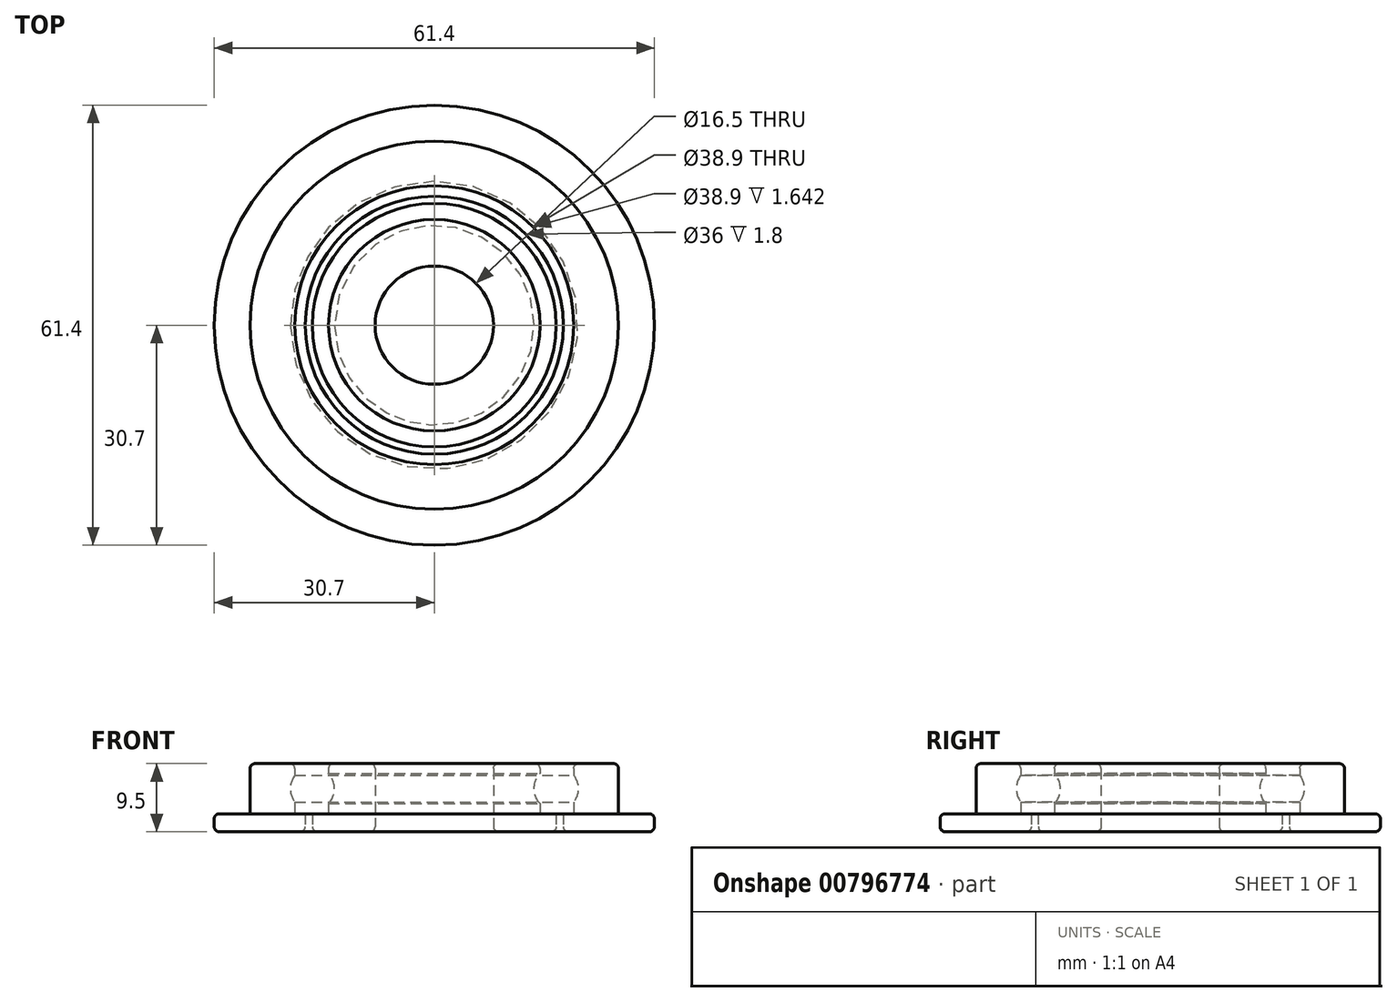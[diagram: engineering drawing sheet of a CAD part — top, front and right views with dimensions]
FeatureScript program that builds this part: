
annotation { "Feature Type Name" : "Feature", "Feature Type Description" : "" }
export const myFeature = defineFeature(function(context is Context, id is Id, definition is map)
    precondition{}
    {
        {
            var Q0;
            Q0=qCreatedBy(makeId("Front.planeOp"),FACE);
            var sketch = newSketch(context, id + "F0", { "sketchPlane" : qUnion([Q0])});
            skLineSegment(sketch, "E0.bottom", {"start": v(8.25, 3.5) * mm, "end": v(14.75, 3.5) * mm});
            skLineSegment(sketch, "E0.top", {"start": v(8.25, -3.5) * mm, "end": v(14.75, -3.5) * mm});
            skLineSegment(sketch, "E0.left", {"start": v(8.25, 3.5) * mm, "end": v(8.25, -3.5) * mm});
            skLineSegment(sketch, "E0.right", {"start": v(14.75, 3.5) * mm, "end": v(14.75, -3.5) * mm});
            skLineSegment(sketch, "E1.bottom", {"start": v(19.45, -3.5) * mm, "end": v(25.7, -3.5) * mm});
            skLineSegment(sketch, "E1.top", {"start": v(19.45, 3.5) * mm, "end": v(25.7, 3.5) * mm});
            skLineSegment(sketch, "E1.left", {"start": v(19.45, -3.5) * mm, "end": v(19.45, 3.5) * mm});
            skLineSegment(sketch, "E1.right", {"start": v(25.7, -3.5) * mm, "end": v(25.7, 3.5) * mm});
            skCircle(sketch, "E2", {"center": v(17, 0) * mm, "radius": 3.08 * mm});
            skLineSegment(sketch, "E3", {"start": v(0, 0) * mm, "end": v(0, 9.43) * mm, "construction": true});
            skLineSegment(sketch, "E4.bottom", {"start": v(8.25, -3.5) * mm, "end": v(17, -3.5) * mm});
            skLineSegment(sketch, "E4.top", {"start": v(8.25, -6) * mm, "end": v(17, -6) * mm});
            skLineSegment(sketch, "E4.left", {"start": v(8.25, -3.5) * mm, "end": v(8.25, -6) * mm});
            skLineSegment(sketch, "E4.right", {"start": v(17, -3.5) * mm, "end": v(17, -6) * mm});
            skLineSegment(sketch, "E5.bottom", {"start": v(8.25, 3.5) * mm, "end": v(10.25, 3.5) * mm});
            skLineSegment(sketch, "E5.top", {"start": v(8.25, 8.5) * mm, "end": v(10.25, 8.5) * mm});
            skLineSegment(sketch, "E5.left", {"start": v(8.25, 3.5) * mm, "end": v(8.25, 8.5) * mm});
            skLineSegment(sketch, "E5.right", {"start": v(10.25, 3.5) * mm, "end": v(10.25, 8.5) * mm});
            skLineSegment(sketch, "E6.bottom", {"start": v(18, -3.5) * mm, "end": v(30.7, -3.5) * mm});
            skLineSegment(sketch, "E6.top", {"start": v(18, -6) * mm, "end": v(30.7, -6) * mm});
            skLineSegment(sketch, "E6.left", {"start": v(18, -3.5) * mm, "end": v(18, -6) * mm});
            skLineSegment(sketch, "E6.right", {"start": v(30.7, -3.5) * mm, "end": v(30.7, -6) * mm});
            skSolve(sketch);
        }
        {
            var Q0;
            {var subQ1=sQuery(id+"F0.wireOp",EDGE,"E0.bottom");Q0=makeQuery(id+"F0.imprint","IMPRINT",FACE,{"disambiguationData":[TD([[makeQuery(id+"F0.imprint","IMPRINT",EDGE,{"derivedFrom":subQ1}),-1.0]])]});}
            var Q1;
            {var subQ4=sQuery(id+"F0.wireOp",EDGE,"E1.bottom");Q1=makeQuery(id+"F0.imprint","IMPRINT",FACE,{"disambiguationData":[TD([[makeQuery(id+"F0.imprint","IMPRINT",EDGE,{"derivedFrom":subQ4}),1.0]])]});}
            var Q2;
            Q2=makeQuery(id+"F0.imprint","IMPRINT",FACE,{"disambiguationData":[TD([[makeQuery(id+"F0.imprint","IMPRINT",EDGE,{"derivedFrom":sQuery(id+"F0.wireOp",EDGE,"E5.bottom")}),1.0]])]});
            var Q3;
            {var subQ2=sQuery(id+"F0.wireOp",EDGE,"E1.top");Q3=makeQuery(id+"F0.imprint","IMPRINT",FACE,{"disambiguationData":[TD([[makeQuery(id+"F0.imprint","IMPRINT",EDGE,{"derivedFrom":subQ2}),-1.0]])]});}
            var Q4;
            Q4=makeQuery(id+"F0.imprint","IMPRINT",FACE,{"disambiguationData":[TD([[makeQuery(id+"F0.imprint","IMPRINT",EDGE,{"derivedFrom":sQuery(id+"F0.wireOp",EDGE,"E4.top")}),1.0]])]});
            var Q5;
            Q5=makeQuery(id+"F0.imprint","IMPRINT",FACE,{"disambiguationData":[TD([[makeQuery(id+"F0.imprint","IMPRINT",EDGE,{"derivedFrom":sQuery(id+"F0.wireOp",EDGE,"E6.top")}),1.0]])]});
            var Q6;
            Q6=sQuery(id+"F0.wireOp",EDGE,"E3");
            revolve(context, id + "F1", {"surfaceOperationType" : NewSurfaceOperationType.NEW, "entities" : qUnion([Q0, Q1, Q2, Q3, Q4, Q5]), "axis" : qUnion([Q6]), "revolveType" : RevolveType.FULL});
        }
        {
            var Q0;
            Q0=makeQuery(id+"F1.opRevolve","SWEPT_EDGE",EDGE,{"disambiguationData":[OSD([sQuery(id+"F0.wireOp",EDGE,"E4.top"),sQuery(id+"F0.wireOp",EDGE,"E4.left")])]});
            var Q1;
            Q1=makeQuery(id+"F1.opRevolve","SWEPT_EDGE",EDGE,{"disambiguationData":[OSD([sQuery(id+"F0.wireOp",EDGE,"E4.top"),sQuery(id+"F0.wireOp",EDGE,"E4.right")])]});
            var Q2;
            Q2=makeQuery(id+"F1.opRevolve","SWEPT_EDGE",EDGE,{"disambiguationData":[OSD([sQuery(id+"F0.wireOp",EDGE,"E6.top"),sQuery(id+"F0.wireOp",EDGE,"E6.left")])]});
            var Q3;
            Q3=makeQuery(id+"F1.opRevolve","SWEPT_EDGE",EDGE,{"disambiguationData":[OSD([sQuery(id+"F0.wireOp",EDGE,"E6.top"),sQuery(id+"F0.wireOp",EDGE,"E6.right")])]});
            var Q4;
            Q4=makeQuery(id+"F1.opRevolve","SWEPT_EDGE",EDGE,{"disambiguationData":[OSD([sQuery(id+"F0.wireOp",EDGE,"E6.bottom"),sQuery(id+"F0.wireOp",EDGE,"E6.right")])]});
            var Q5;
            Q5=makeQuery(id+"F1.opRevolve","SWEPT_EDGE",EDGE,{"disambiguationData":[OSD([sQuery(id+"F0.wireOp",EDGE,"E1.top"),sQuery(id+"F0.wireOp",EDGE,"E1.right")])]});
            var Q6;
            Q6=makeQuery(id+"F1.opRevolve","SWEPT_EDGE",EDGE,{"disambiguationData":[OSD([sQuery(id+"F0.wireOp",EDGE,"E1.top"),sQuery(id+"F0.wireOp",EDGE,"E1.left")])]});
            var Q7;
            Q7=makeQuery(id+"F1.opRevolve","SWEPT_EDGE",EDGE,{"disambiguationData":[OSD([sQuery(id+"F0.wireOp",EDGE,"E0.bottom"),sQuery(id+"F0.wireOp",EDGE,"E0.right")])]});
            var Q8;
            Q8=makeQuery(id+"F1.opRevolve","SWEPT_EDGE",EDGE,{"disambiguationData":[OSD([sQuery(id+"F0.wireOp",EDGE,"E0.bottom"),sQuery(id+"F0.wireOp",EDGE,"E5.bottom"),sQuery(id+"F0.wireOp",EDGE,"E5.right")])]});
            var Q9;
            Q9=makeQuery(id+"F1.opRevolve","SWEPT_EDGE",EDGE,{"disambiguationData":[OSD([sQuery(id+"F0.wireOp",EDGE,"E5.top"),sQuery(id+"F0.wireOp",EDGE,"E5.right")])]});
            var Q10;
            Q10=makeQuery(id+"F1.opRevolve","SWEPT_EDGE",EDGE,{"disambiguationData":[OSD([sQuery(id+"F0.wireOp",EDGE,"E5.top"),sQuery(id+"F0.wireOp",EDGE,"E5.left")])]});
            fillet(context, id + "F2", {"entities" : qUnion([Q0, Q1, Q2, Q3, Q4, Q5, Q6, Q7, Q8, Q9, Q10]), "radius" : .7 * mm, "tangentPropagation" : true, "allowEdgeOverflow" : false});
        }
    });
